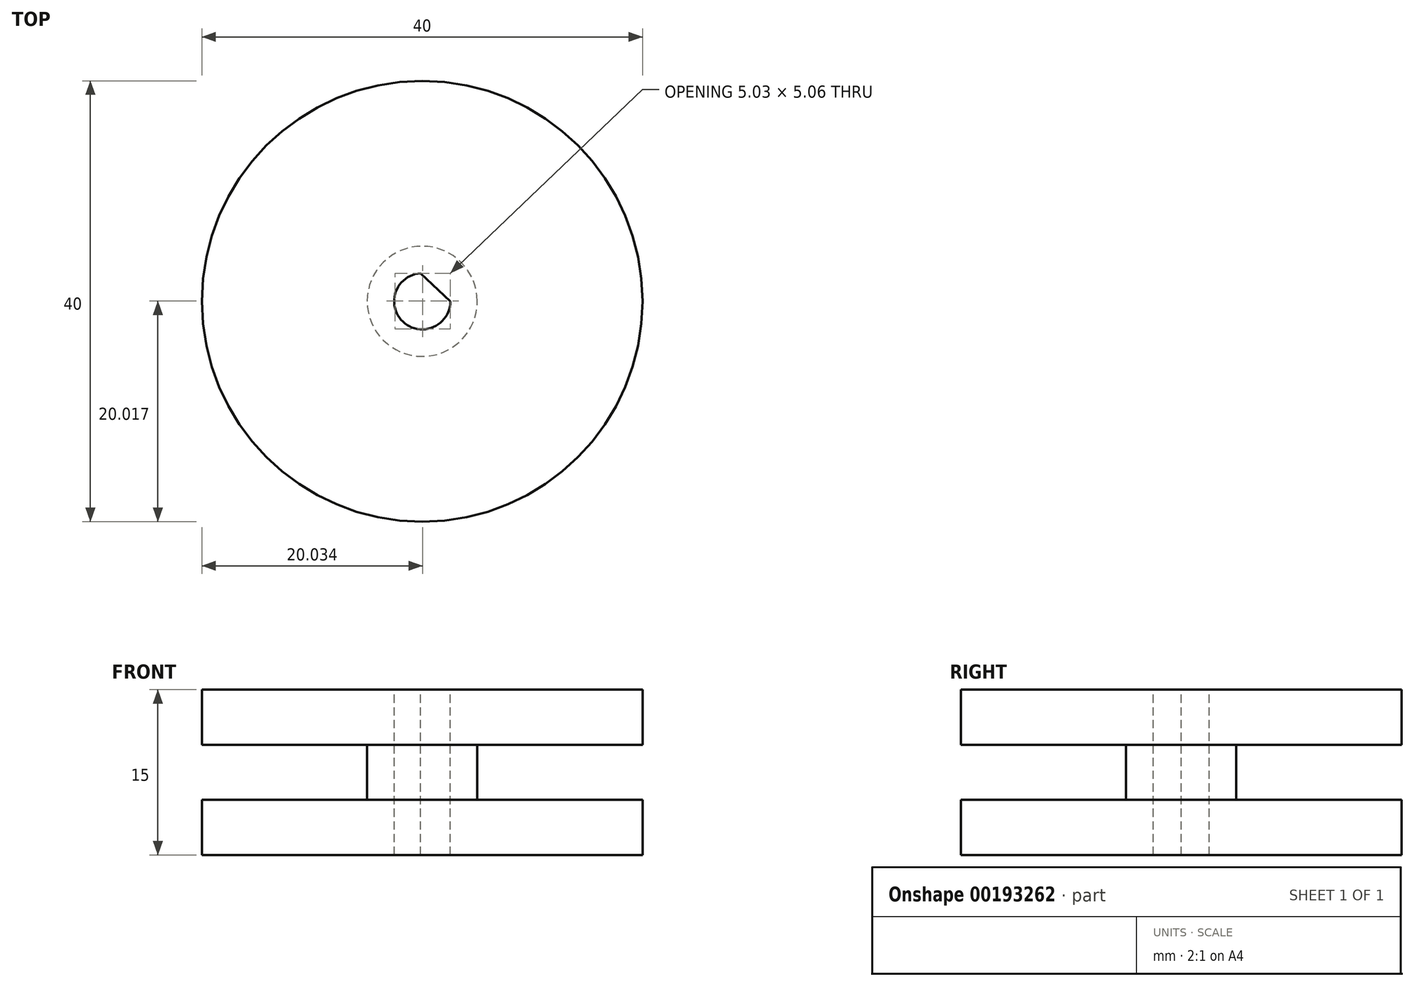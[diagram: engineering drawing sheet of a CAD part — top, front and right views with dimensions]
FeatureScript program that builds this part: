
annotation { "Feature Type Name" : "Feature", "Feature Type Description" : "" }
export const myFeature = defineFeature(function(context is Context, id is Id, definition is map)
    precondition{}
    {
        {
            var Q0;
            Q0=qCreatedBy(makeId("Top.planeOp"),FACE);
            var sketch = newSketch(context, id + "F0", { "sketchPlane" : qUnion([Q0])});
            skCircle(sketch, "E0", {"center": v(0, 0) * mm, "radius": 20 * mm});
            skSolve(sketch);
        }
        {
            var Q0;
            Q0 = qSketchRegion(id + "F0", true);
            extrude(context, id + "F1", {"entities" : qUnion([Q0]), "depth" : 5 * mm});
        }
        {
            var Q0;
            Q0=makeQuery(id+"F1.opExtrude","CAP_FACE",FACE,{"disambiguationData":[OSD([sQuery(id+"F0.wireOp",EDGE,"E0")])],"isStart":false});
            var sketch = newSketch(context, id + "F2", { "sketchPlane" : qUnion([Q0])});
            skCircle(sketch, "E1", {"center": v(0, 0) * mm, "radius": 5 * mm});
            skSolve(sketch);
        }
        {
            var Q0;
            Q0 = qSketchRegion(id + "F2", true);
            extrude(context, id + "F3", {"entities" : qUnion([Q0]), "operationType" : NewBodyOperationType.ADD, "depth" : 5 * mm});
        }
        {
            var Q0;
            Q0=makeQuery(id+"F3.opExtrude","CAP_FACE",FACE,{"disambiguationData":[OSD([sQuery(id+"F2.wireOp",EDGE,"E1")])],"isStart":false});
            var sketch = newSketch(context, id + "F4", { "sketchPlane" : qUnion([Q0])});
            skCircle(sketch, "E2", {"center": v(0, 0) * mm, "radius": 20 * mm});
            skSolve(sketch);
        }
        {
            var Q0;
            Q0 = qSketchRegion(id + "F4", true);
            extrude(context, id + "F5", {"entities" : qUnion([Q0]), "operationType" : NewBodyOperationType.ADD, "depth" : 5 * mm});
        }
        {
            var Q0;
            Q0=makeQuery(id+"F5.opExtrude","CAP_FACE",FACE,{"disambiguationData":[OSD([sQuery(id+"F4.wireOp",EDGE,"E2")])],"isStart":false});
            var sketch = newSketch(context, id + "F6", { "sketchPlane" : qUnion([Q0])});
            skCircle(sketch, "E3", {"center": v(0, 0) * mm, "radius": 2.55 * mm});
            skLineSegment(sketch, "E4", {"start": v(-0.15, 2.55) * mm, "end": v(2.55, 0) * mm});
            skSolve(sketch);
        }
        {
            var Q0;
            {var subQ0=sQuery(id+"F6.wireOp",EDGE,"E4");Q0=makeQuery(id+"F6.imprint","IMPRINT",FACE,{"disambiguationData":[TD([[makeQuery(id+"F6.imprint","IMPRINT",EDGE,{"derivedFrom":subQ0}),-1.0]])]});}
            extrude(context, id + "F7", {"entities" : qUnion([Q0]), "operationType" : NewBodyOperationType.REMOVE, "oppositeDirection" : true, "depth" : 25 * mm});
        }
    });
